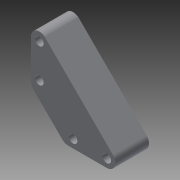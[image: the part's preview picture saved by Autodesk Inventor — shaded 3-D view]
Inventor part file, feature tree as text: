
AUTODESK INVENTOR PART (.ipt)
format: ipt  version: 2014 (Build 180170000, 170)  size: 94,720 bytes
history: native  units: in
note: dims shown in document units (in); Inventor stores cm internally (conversion verified against a paired STEP export)
features: extrude x1, sketch x1
ambient origin geometry x8: Origin, YZ Plane, XZ Plane, XY Plane, X Axis, Y Axis, Z Axis, Center Point
bodies: Solid1 (feature_tree)
feature tree (2):
  extrude  "Extrusion1"  Depth=0.25in
  sketch  "Sketch1"  dims[d6=0.25in d7=0.25in d8=0.25in d9=0.25in d10=0.25in d11=1.0in d12=0.0in]
